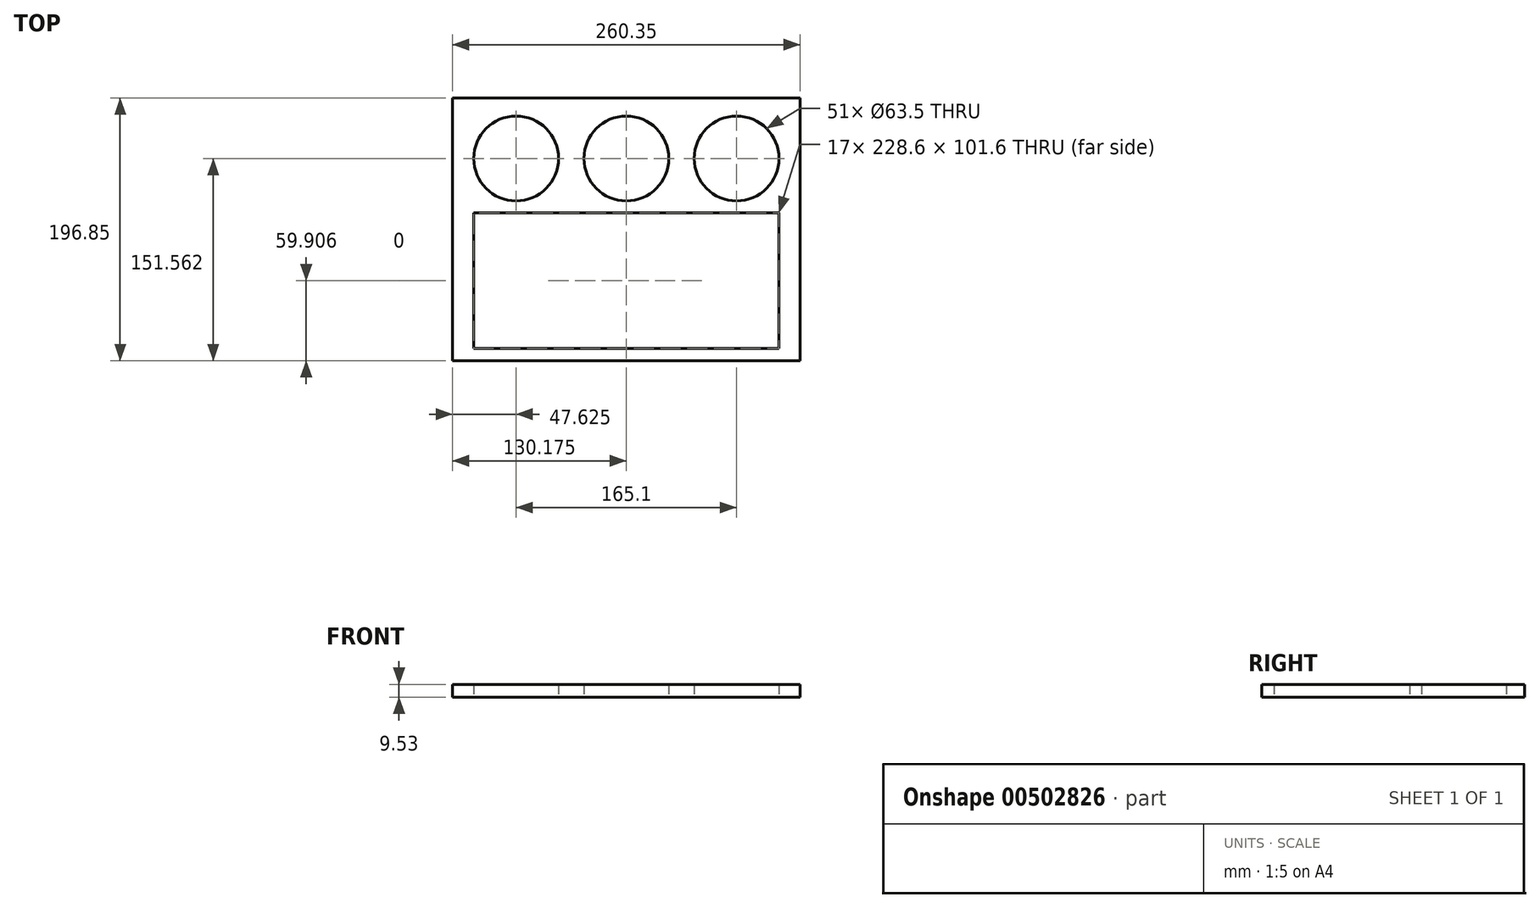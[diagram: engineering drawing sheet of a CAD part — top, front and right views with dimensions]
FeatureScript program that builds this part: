
annotation { "Feature Type Name" : "Feature", "Feature Type Description" : "" }
export const myFeature = defineFeature(function(context is Context, id is Id, definition is map)
    precondition{}
    {
        {
            var Q0;
            Q0=qCreatedBy(makeId("Top.planeOp"),FACE);
            var sketch = newSketch(context, id + "F0", { "sketchPlane" : qUnion([Q0])});
            skLineSegment(sketch, "E0.bottom", {"start": v(0, 0) * mm, "end": v(260.35, 0) * mm});
            skLineSegment(sketch, "E0.top", {"start": v(0, -196.85) * mm, "end": v(260.35, -196.85) * mm});
            skLineSegment(sketch, "E0.left", {"start": v(0, 0) * mm, "end": v(0, -196.85) * mm});
            skLineSegment(sketch, "E0.right", {"start": v(260.35, 0) * mm, "end": v(260.35, -196.85) * mm});
            skCircle(sketch, "E1", {"center": v(47.62, -45.29) * mm, "radius": 31.75 * mm});
            skCircle(sketch, "E2", {"center": v(130.18, -45.29) * mm, "radius": 31.75 * mm});
            skCircle(sketch, "E3", {"center": v(212.73, -45.29) * mm, "radius": 31.75 * mm});
            skLineSegment(sketch, "E4.bottom", {"start": v(15.88, -86.14) * mm, "end": v(244.48, -86.14) * mm});
            skLineSegment(sketch, "E4.top", {"start": v(15.88, -187.74) * mm, "end": v(244.48, -187.74) * mm});
            skLineSegment(sketch, "E4.left", {"start": v(15.88, -86.14) * mm, "end": v(15.88, -187.74) * mm});
            skLineSegment(sketch, "E4.right", {"start": v(244.48, -86.14) * mm, "end": v(244.48, -187.74) * mm});
            skSolve(sketch);
        }
        {
            var Q0;
            Q0=makeQuery(id+"F0.imprint","IMPRINT",FACE,{"disambiguationData":[TD([[makeQuery(id+"F0.imprint","IMPRINT",EDGE,{"derivedFrom":sQuery(id+"F0.wireOp",EDGE,"E0.bottom")}),-1.0]])]});
            extrude(context, id + "F1", {"entities" : qUnion([Q0]), "depth" : 9.52 * mm, "offsetDistance" : 25.4 * mm});
        }
    });
